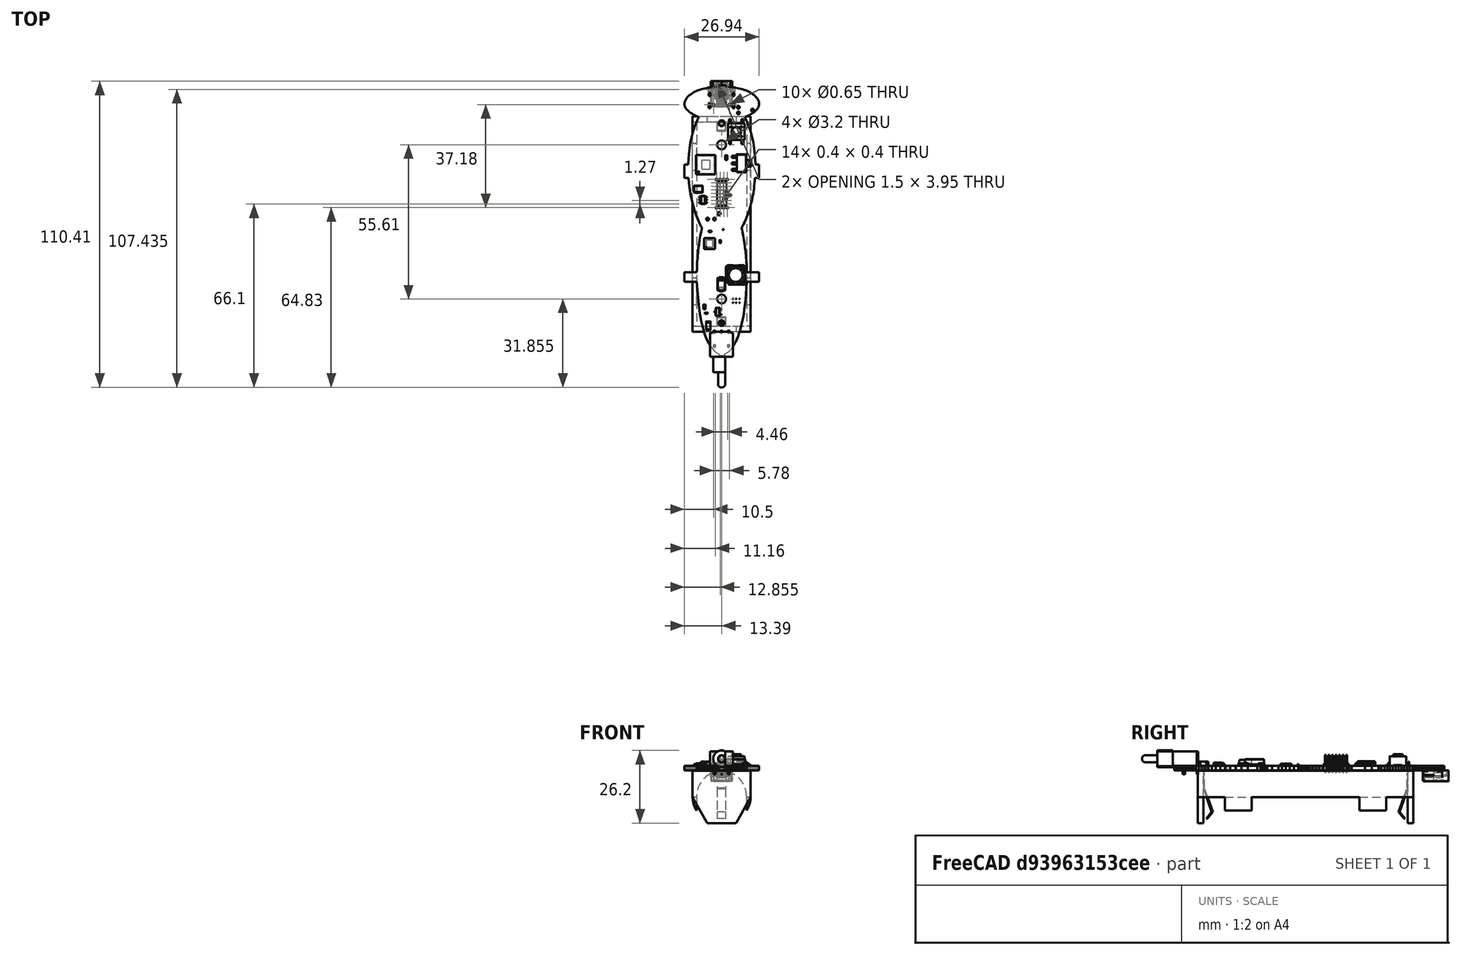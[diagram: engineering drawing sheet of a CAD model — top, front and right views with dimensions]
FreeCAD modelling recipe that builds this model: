
FCSTD DOCUMENT  (FreeCAD 0.21R30454 (Git))
Label: WholeBadge
License: All rights reserved
LicenseURL: http://en.wikipedia.org/wiki/All_rights_reserved
objects: App::Link×64, Part::Feature×20, App::Part×5, PartDesign::CoordinateSystem×1, Sketcher::SketchObject×1
note: 22 computed .brp shape members not serialized (recipe doc carries the construction recipe); baked Part::Feature solids carry a one-line shape summary decoded from their .brp

FEATURE [PartDesign::CoordinateSystem] Local_CS_931
  AttacherType = Attacher::AttachEngine3D
  MapMode = 2
  Support = -> [X_Axis001]
FEATURE [Part::Feature] Pcb_931
  shape: bbox 26.94 x 97.45 x 1.6 mm, 316 faces (baked)
FEATURE [Sketcher::SketchObject] PCB_Sketch_931
  FullyConstrained = false
  sketch-geometry (258):
    g0: LineSegment StartX=204.611 StartY=-59.7706 StartZ=0 EndX=204.161 EndY=-58.747 EndZ=0
    g1: LineSegment StartX=207.307 StartY=-79.6422 StartZ=0 EndX=208.849 EndY=-79.6422 EndZ=0
    g2: LineSegment StartX=203.133 StartY=-100.504 StartZ=0 EndX=202.842 EndY=-99.0355 EndZ=0
    g3: LineSegment StartX=198.204 StartY=-141.964 StartZ=0 EndX=198.335 EndY=-141.829 EndZ=0
    g4: LineSegment StartX=196.821 StartY=-46.2543 StartZ=0 EndX=195.381 EndY=-46.2543 EndZ=0
    g5: LineSegment StartX=186.994 StartY=-104.828 StartZ=0 EndX=186.849 EndY=-106.147 EndZ=0
    g6: LineSegment StartX=190.699 StartY=-139.374 StartZ=0 EndX=191.002 EndY=-139.905 EndZ=0
    g7: LineSegment StartX=194.282 StartY=-143.161 StartZ=0 EndX=194.282 EndY=-143.702 EndZ=0
    g8: LineSegment StartX=206.155 StartY=-49.1673 StartZ=0 EndX=205.642 EndY=-48.8567 EndZ=0
    g9: LineSegment StartX=207.546 StartY=-55.4632 StartZ=0 EndX=207.833 EndY=-55.1801 EndZ=0
    g10: LineSegment StartX=191.879 StartY=-141.193 StartZ=0 EndX=192.157 EndY=-141.532 EndZ=0
    g11: LineSegment StartX=186.361 StartY=-117.075 StartZ=0 EndX=186.651 EndY=-121.509 EndZ=0
    g12: LineSegment StartX=208.789 StartY=-53.5041 StartZ=0 EndX=208.834 EndY=-53.2317 EndZ=0
    g13: LineSegment StartX=206.019 StartY=-88.581 StartZ=0 EndX=206.204 EndY=-87.8001 EndZ=0
    g14: LineSegment StartX=203.931 StartY=-123.5 StartZ=0 EndX=204.11 EndY=-121.509 EndZ=0
    g15: LineSegment StartX=183.585 StartY=-81.6183 StartZ=0 EndX=183.791 EndY=-83.5056 EndZ=0
    g16: LineSegment StartX=201.902 StartY=-134.849 StartZ=0 EndX=202.197 EndY=-133.815 EndZ=0
    g17: LineSegment StartX=202.746 StartY=-97.2753 StartZ=0 EndX=202.978 EndY=-96.8717 EndZ=0
    g18: LineSegment StartX=202.76 StartY=-131.45 StartZ=0 EndX=203.025 EndY=-130.106 EndZ=0
    g19: LineSegment StartX=184.261 StartY=-65.7953 StartZ=0 EndX=184.058 EndY=-66.826 EndZ=0
    g20: LineSegment StartX=202.505 StartY=-97.6016 StartZ=0 EndX=202.585 EndY=-97.5204 EndZ=0
    g21: LineSegment StartX=196.48 StartY=-143.161 StartZ=0 EndX=196.623 EndY=-143.098 EndZ=0
    g22: LineSegment StartX=185.289 StartY=-56.8742 StartZ=0 EndX=185.841 EndY=-57.153 EndZ=0
    g23: LineSegment StartX=208.834 StartY=-53.2317 StartZ=0 EndX=208.851 EndY=-52.9624 EndZ=0
    g24: LineSegment StartX=204.4 StartY=-117.075 StartZ=0 EndX=208.849 EndY=-117.075 EndZ=0
    g25: LineSegment StartX=185.651 StartY=-48.576 StartZ=0 EndX=185.119 EndY=-48.8567 EndZ=0
    g26: LineSegment StartX=200.369 StartY=-138.788 StartZ=0 EndX=200.678 EndY=-138.143 EndZ=0
    g27: LineSegment StartX=185.964 StartY=-92.6642 StartZ=0 EndX=186.78 EndY=-94.7637 EndZ=0
    g28: LineSegment StartX=198.468 StartY=-141.686 StartZ=0 EndX=198.604 EndY=-141.532 EndZ=0
    g29: LineSegment StartX=200.262 StartY=-47.1518 StartZ=0 EndX=199.594 EndY=-47.0453 EndZ=0
    g30: LineSegment StartX=186.393 StartY=-112.527 StartZ=0 EndX=186.377 EndY=-113.724 EndZ=0
    g31: LineSegment StartX=182.209 StartY=-51.6716 StartZ=0 EndX=182.103 EndY=-51.9211 EndZ=0
    g32: LineSegment StartX=187.169 StartY=-103.429 StartZ=0 EndX=186.994 EndY=-104.828 EndZ=0
    g33: LineSegment StartX=197.156 StartY=-142.81 StartZ=0 EndX=197.366 EndY=-142.672 EndZ=0
    g34: LineSegment StartX=203.992 StartY=-48.0954 StartZ=0 EndX=203.408 EndY=-47.8915 EndZ=0
    g35: LineSegment StartX=200.678 StartY=-138.143 StartZ=0 EndX=200.987 EndY=-137.433 EndZ=0
    g36: LineSegment StartX=191.301 StartY=-140.383 StartZ=0 EndX=191.593 EndY=-140.811 EndZ=0
    g37: LineSegment StartX=186.503 StartY=-110.129 StartZ=0 EndX=186.46 EndY=-110.807 EndZ=0
    g38: LineSegment StartX=183.377 StartY=-72.3896 StartZ=0 EndX=183.215 EndY=-74.8986 EndZ=0
    g39: LineSegment StartX=206.647 StartY=-49.5098 StartZ=0 EndX=206.155 EndY=-49.1673 EndZ=0
    g40: LineSegment StartX=201.601 StartY=-135.792 StartZ=0 EndX=201.902 EndY=-134.849 EndZ=0
    g41: LineSegment StartX=203.408 StartY=-47.8915 StartZ=0 EndX=202.807 EndY=-47.709 EndZ=0
    g42: LineSegment StartX=208.428 StartY=-51.4271 StartZ=0 EndX=208.284 EndY=-51.188 EndZ=0
    g43: LineSegment StartX=182.294 StartY=-54.3351 StartZ=0 EndX=182.469 EndY=-54.6157 EndZ=0
    g44: LineSegment StartX=185.119 StartY=-48.8567 StartZ=0 EndX=184.607 EndY=-49.1673 EndZ=0
    g45: LineSegment StartX=204.382 StartY=-93.7798 StartZ=0 EndX=204.798 EndY=-92.6642 EndZ=0
    g46: LineSegment StartX=183.215 StartY=-74.8986 StartZ=0 EndX=181.912 EndY=-74.8986 EndZ=0
    g47: LineSegment StartX=205.216 StartY=-91.4223 StartZ=0 EndX=205.627 EndY=-90.0595 EndZ=0
    g48: LineSegment StartX=208.849 StartY=-74.8986 StartZ=0 EndX=207.546 EndY=-74.8986 EndZ=0
    g49: LineSegment StartX=186.651 StartY=-121.509 StartZ=0 EndX=187.031 EndY=-125.349 EndZ=0
    g50: LineSegment StartX=204.125 StartY=-108.431 StartZ=0 EndX=203.913 EndY=-106.147 EndZ=0
    g51: LineSegment StartX=187.38 StartY=-101.978 StartZ=0 EndX=187.169 EndY=-103.429 EndZ=0
    g52: LineSegment StartX=183.913 StartY=-56.0295 StartZ=0 EndX=184.326 EndY=-56.3121 EndZ=0
    g53: LineSegment StartX=205.11 StartY=-48.576 StartZ=0 EndX=204.56 EndY=-48.3229 EndZ=0
    g54: LineSegment StartX=201.561 StartY=-47.4 StartZ=0 EndX=200.918 EndY=-47.2693 EndZ=0
    g55: LineSegment StartX=204.258 StartY=-110.129 StartZ=0 EndX=204.2 EndY=-109.347 EndZ=0
    g56: LineSegment StartX=193.978 StartY=-143.02 StartZ=0 EndX=194.282 EndY=-143.161 EndZ=0
    g57: LineSegment StartX=181.958 StartY=-52.4338 StartZ=0 EndX=181.922 EndY=-52.6963 EndZ=0
    g58: LineSegment StartX=204.798 StartY=-92.6642 StartZ=0 EndX=205.216 EndY=-91.4223 EndZ=0
    g59: LineSegment StartX=204.302 StartY=-110.807 StartZ=0 EndX=204.258 EndY=-110.129 EndZ=0
    g60: LineSegment StartX=196.623 StartY=-143.098 StartZ=0 EndX=196.784 EndY=-143.02 EndZ=0
    g61: LineSegment StartX=198.227 StartY=-46.857 StartZ=0 EndX=196.821 EndY=-46.6878 EndZ=0
    g62: LineSegment StartX=204.56 StartY=-48.3229 StartZ=0 EndX=203.992 EndY=-48.0954 EndZ=0
    g63: LineSegment StartX=183.726 StartY=-68.9546 StartZ=0 EndX=183.593 EndY=-70.0623 EndZ=0
    g64: LineSegment StartX=200.215 StartY=-139.088 StartZ=0 EndX=200.369 EndY=-138.788 EndZ=0
    g65: LineSegment StartX=207.117 StartY=-49.8853 StartZ=0 EndX=206.647 EndY=-49.5098 EndZ=0
    g66: LineSegment StartX=181.972 StartY=-53.5041 StartZ=0 EndX=182.047 EndY=-53.779 EndZ=0
    g67: LineSegment StartX=184.607 StartY=-49.1673 StartZ=0 EndX=184.114 EndY=-49.5098 EndZ=0
    g68: LineSegment StartX=199.61 StartY=-140.15 StartZ=0 EndX=199.759 EndY=-139.905 EndZ=0
    g69: LineSegment StartX=205.627 StartY=-90.0595 StartZ=0 EndX=206.019 EndY=-88.581 EndZ=0
    g70: LineSegment StartX=202.679 StartY=-98.3125 StartZ=0 EndX=202.505 EndY=-97.6016 EndZ=0
    g71: LineSegment StartX=196.962 StartY=-142.925 StartZ=0 EndX=197.156 EndY=-142.81 EndZ=0
    g72: LineSegment StartX=206.204 StartY=-87.8001 StartZ=0 EndX=206.381 EndY=-86.9923 EndZ=0
    g73: LineSegment StartX=198.604 StartY=-141.532 StartZ=0 EndX=198.742 EndY=-141.368 EndZ=0
    g74: LineSegment StartX=189.774 StartY=-137.433 StartZ=0 EndX=190.393 EndY=-138.788 EndZ=0
    g75: LineSegment StartX=184.058 StartY=-66.826 StartZ=0 EndX=183.88 EndY=-67.8774 EndZ=0
    g76: LineSegment StartX=189.16 StartY=-135.792 StartZ=0 EndX=189.774 EndY=-137.433 EndZ=0
    g77: LineSegment StartX=186.151 StartY=-59.7706 StartZ=0 EndX=185.743 EndY=-60.7805 EndZ=0
    g78: LineSegment StartX=206.381 StartY=-86.9923 StartZ=0 EndX=206.547 EndY=-86.1583 EndZ=0
    g79: LineSegment StartX=208.84 StartY=-52.6963 StartZ=0 EndX=208.803 EndY=-52.4338 EndZ=0
    g80: LineSegment StartX=204.318 StartY=-57.4299 StartZ=0 EndX=204.92 EndY=-57.153 EndZ=0
    g81: LineSegment StartX=188.015 StartY=-97.2753 StartZ=0 EndX=188.257 EndY=-97.6016 EndZ=0
    g82: LineSegment StartX=205.472 StartY=-56.8742 StartZ=0 EndX=205.977 EndY=-56.5938 EndZ=0
    g83: LineSegment StartX=185.134 StartY=-90.0595 StartZ=0 EndX=185.545 EndY=-91.4223 EndZ=0
    g84: LineSegment StartX=203.512 StartY=-127.062 StartZ=0 EndX=203.731 EndY=-125.349 EndZ=0
    g85: LineSegment StartX=202.807 StartY=-47.709 StartZ=0 EndX=202.191 EndY=-47.5458 EndZ=0
    g86: LineSegment StartX=189.843 StartY=-47.2693 StartZ=0 EndX=189.2 EndY=-47.4 EndZ=0
    g87: LineSegment StartX=203.025 StartY=-130.106 StartZ=0 EndX=203.276 EndY=-128.645 EndZ=0
    g88: LineSegment StartX=199.314 StartY=-140.603 StartZ=0 EndX=199.461 EndY=-140.383 EndZ=0
    g89: LineSegment StartX=207.169 StartY=-70.0623 StartZ=0 EndX=207.035 EndY=-68.9546 EndZ=0
    g90: LineSegment StartX=199.461 StartY=-140.383 StartZ=0 EndX=199.61 EndY=-140.15 EndZ=0
    g91: LineSegment StartX=191.002 StartY=-139.905 StartZ=0 EndX=191.301 EndY=-140.383 EndZ=0
    g92: LineSegment StartX=186.46 StartY=-110.807 StartZ=0 EndX=186.429 EndY=-111.412 EndZ=0
    g93: LineSegment StartX=182.638 StartY=-50.9546 StartZ=0 EndX=182.477 EndY=-51.188 EndZ=0
    g94: LineSegment StartX=196.821 StartY=-46.6878 StartZ=0 EndX=196.821 EndY=-46.2543 EndZ=0
    g95: LineSegment StartX=183.543 StartY=-55.7465 StartZ=0 EndX=183.913 EndY=-56.0295 EndZ=0
    g96: LineSegment StartX=181.912 StartY=-117.075 StartZ=0 EndX=186.361 EndY=-117.075 EndZ=0
    g97: LineSegment StartX=204.2 StartY=-109.347 StartZ=0 EndX=204.125 EndY=-108.431 EndZ=0
    g98: LineSegment StartX=181.911 StartY=-52.9624 StartZ=0 EndX=181.927 EndY=-53.2317 EndZ=0
    g99: LineSegment StartX=206.702 StartY=-85.2987 StartZ=0 EndX=206.844 EndY=-84.4142 EndZ=0
    g100: LineSegment StartX=208.742 StartY=-52.1753 StartZ=0 EndX=208.658 EndY=-51.9211 EndZ=0
    g101: LineSegment StartX=192.686 StartY=-142.089 StartZ=0 EndX=192.935 EndY=-142.314 EndZ=0
    g102: LineSegment StartX=187.095 StartY=-57.7046 StartZ=0 EndX=186.6 EndY=-58.747 EndZ=0
    g103: LineSegment StartX=208.849 StartY=-117.075 StartZ=0 EndX=208.849 EndY=-113.724 EndZ=0
    g104: LineSegment StartX=196.784 StartY=-143.02 StartZ=0 EndX=196.962 EndY=-142.925 EndZ=0
    g105: LineSegment StartX=186.6 StartY=-58.747 StartZ=0 EndX=186.151 EndY=-59.7706 EndZ=0
    g106: LineSegment StartX=184.785 StartY=-56.5938 StartZ=0 EndX=185.289 EndY=-56.8742 EndZ=0
    g107: LineSegment StartX=198.882 StartY=-141.193 StartZ=0 EndX=199.024 EndY=-141.008 EndZ=0
    g108: LineSegment StartX=191.167 StartY=-47.0453 StartZ=0 EndX=189.843 EndY=-47.2693 EndZ=0
    g109: LineSegment StartX=182.103 StartY=-51.9211 StartZ=0 EndX=182.019 EndY=-52.1753 EndZ=0
    g110: LineSegment StartX=200.918 StartY=-47.2693 StartZ=0 EndX=200.262 EndY=-47.1518 EndZ=0
    g111: LineSegment StartX=203.268 StartY=-96.315 StartZ=0 EndX=203.607 EndY=-95.6105 EndZ=0
    g112: LineSegment StartX=188.565 StartY=-133.815 StartZ=0 EndX=189.16 EndY=-135.792 EndZ=0
    g113: LineSegment StartX=207.218 StartY=-55.7465 StartZ=0 EndX=207.546 EndY=-55.4632 EndZ=0
    g114: LineSegment StartX=207.252 StartY=-80.641 StartZ=0 EndX=207.307 EndY=-79.6422 EndZ=0
    g115: LineSegment StartX=188.257 StartY=-97.6016 StartZ=0 EndX=187.92 EndY=-99.0355 EndZ=0
    g116: LineSegment StartX=186.443 StartY=-57.4299 StartZ=0 EndX=187.095 EndY=-57.7046 EndZ=0
    g117: LineSegment StartX=203.607 StartY=-95.6105 StartZ=0 EndX=203.982 EndY=-94.7637 EndZ=0
    g118: LineSegment StartX=207.554 StartY=-50.2921 StartZ=0 EndX=207.117 EndY=-49.8853 EndZ=0
    g119: LineSegment StartX=185.841 StartY=-57.153 StartZ=0 EndX=186.443 EndY=-57.4299 EndZ=0
    g120: LineSegment StartX=204.267 StartY=-119.37 StartZ=0 EndX=204.4 EndY=-117.075 EndZ=0
    g121: LineSegment StartX=199.168 StartY=-140.811 StartZ=0 EndX=199.314 EndY=-140.603 EndZ=0
    g122: LineSegment StartX=199.91 StartY=-139.646 StartZ=0 EndX=200.062 EndY=-139.374 EndZ=0
    g123: LineSegment StartX=203.731 StartY=-125.349 StartZ=0 EndX=203.931 EndY=-123.5 EndZ=0
    g124: LineSegment StartX=206.844 StartY=-84.4142 StartZ=0 EndX=206.971 EndY=-83.5056 EndZ=0
    g125: LineSegment StartX=203.913 StartY=-106.147 StartZ=0 EndX=203.768 EndY=-104.828 EndZ=0
    g126: LineSegment StartX=206.848 StartY=-56.0295 StartZ=0 EndX=207.218 EndY=-55.7465 EndZ=0
    g127: LineSegment StartX=198.335 StartY=-141.829 StartZ=0 EndX=198.468 EndY=-141.686 EndZ=0
    g128: LineSegment StartX=204.333 StartY=-111.412 StartZ=0 EndX=204.302 EndY=-110.807 EndZ=0
    g129: LineSegment StartX=183.004 StartY=-50.5063 StartZ=0 EndX=182.814 EndY=-50.7272 EndZ=0
    g130: LineSegment StartX=183.88 StartY=-67.8774 StartZ=0 EndX=183.726 EndY=-68.9546 EndZ=0
    g131: LineSegment StartX=181.912 StartY=-79.6422 StartZ=0 EndX=183.454 EndY=-79.6422 EndZ=0
    g132: LineSegment StartX=198.075 StartY=-142.089 StartZ=0 EndX=198.204 EndY=-141.964 EndZ=0
    g133: LineSegment StartX=200.062 StartY=-139.374 StartZ=0 EndX=200.215 EndY=-139.088 EndZ=0
    g134: LineSegment StartX=185.545 StartY=-91.4223 StartZ=0 EndX=185.964 EndY=-92.6642 EndZ=0
    g135: LineSegment StartX=202.978 StartY=-96.8717 StartZ=0 EndX=203.268 EndY=-96.315 EndZ=0
    g136: LineSegment StartX=205.018 StartY=-60.7805 StartZ=0 EndX=204.611 EndY=-59.7706 EndZ=0
    g137: LineSegment StartX=187.954 StartY=-47.709 StartZ=0 EndX=187.354 EndY=-47.8915 EndZ=0
    g138: LineSegment StartX=208.292 StartY=-54.6157 StartZ=0 EndX=208.467 EndY=-54.3351 EndZ=0
    g139: LineSegment StartX=187.92 StartY=-99.0355 StartZ=0 EndX=187.629 EndY=-100.504 EndZ=0
    g140: LineSegment StartX=208.658 StartY=-51.9211 StartZ=0 EndX=208.553 EndY=-51.6716 EndZ=0
    g141: LineSegment StartX=188.002 StartY=-131.45 StartZ=0 EndX=188.565 EndY=-133.815 EndZ=0
    g142: LineSegment StartX=204.11 StartY=-121.509 StartZ=0 EndX=204.267 EndY=-119.37 EndZ=0
    g143: LineSegment StartX=196.48 StartY=-143.702 StartZ=0 EndX=196.48 EndY=-143.161 EndZ=0
    g144: LineSegment StartX=183.791 StartY=-83.5056 StartZ=0 EndX=184.059 EndY=-85.2987 EndZ=0
    g145: LineSegment StartX=193.605 StartY=-142.81 StartZ=0 EndX=193.8 EndY=-142.925 EndZ=0
    g146: LineSegment StartX=186.636 StartY=-108.431 StartZ=0 EndX=186.503 EndY=-110.129 EndZ=0
    g147: LineSegment StartX=192.535 StartY=-46.857 StartZ=0 EndX=191.167 EndY=-47.0453 EndZ=0
    g148: LineSegment StartX=198.742 StartY=-141.368 StartZ=0 EndX=198.882 EndY=-141.193 EndZ=0
    g149: LineSegment StartX=182.814 StartY=-50.7272 StartZ=0 EndX=182.638 EndY=-50.9546 EndZ=0
    g150: LineSegment StartX=187.031 StartY=-125.349 StartZ=0 EndX=187.486 EndY=-128.645 EndZ=0
    g151: LineSegment StartX=183.421 StartY=-50.085 StartZ=0 EndX=183.207 EndY=-50.2921 EndZ=0
    g152: LineSegment StartX=204.368 StartY=-112.527 StartZ=0 EndX=204.354 EndY=-111.975 EndZ=0
    g153: LineSegment StartX=202.585 StartY=-97.5204 StartZ=0 EndX=202.746 EndY=-97.2753 EndZ=0
    g154: LineSegment StartX=184.742 StartY=-88.581 StartZ=0 EndX=185.134 EndY=-90.0595 EndZ=0
    g155: LineSegment StartX=183.454 StartY=-79.6422 StartZ=0 EndX=183.585 EndY=-81.6183 EndZ=0
    g156: LineSegment StartX=206.971 StartY=-83.5056 StartZ=0 EndX=207.082 EndY=-82.5734 EndZ=0
    g157: LineSegment StartX=206.704 StartY=-66.826 StartZ=0 EndX=206.501 EndY=-65.7953 EndZ=0
    g158: LineSegment StartX=203.592 StartY=-103.429 StartZ=0 EndX=203.382 EndY=-101.978 EndZ=0
    g159: LineSegment StartX=208.714 StartY=-53.779 StartZ=0 EndX=208.789 EndY=-53.5041 EndZ=0
    g160: LineSegment StartX=203.276 StartY=-128.645 StartZ=0 EndX=203.512 EndY=-127.062 EndZ=0
    g161: LineSegment StartX=186.429 StartY=-111.412 StartZ=0 EndX=186.393 EndY=-112.527 EndZ=0
    g162: LineSegment StartX=197.826 StartY=-142.314 StartZ=0 EndX=198.075 EndY=-142.089 EndZ=0
    g163: LineSegment StartX=193.396 StartY=-142.672 StartZ=0 EndX=193.605 EndY=-142.81 EndZ=0
    g164: LineSegment StartX=208.851 StartY=-52.9624 StartZ=0 EndX=208.84 EndY=-52.6963 EndZ=0
    g165: LineSegment StartX=197.59 StartY=-142.507 StartZ=0 EndX=197.826 EndY=-142.314 EndZ=0
    g166: LineSegment StartX=206.009 StartY=-63.7765 StartZ=0 EndX=205.715 EndY=-62.7784 EndZ=0
    g167: LineSegment StartX=185.743 StartY=-60.7805 StartZ=0 EndX=185.376 EndY=-61.7814 EndZ=0
    g168: LineSegment StartX=195.381 StartY=-143.702 StartZ=0 EndX=196.48 EndY=-143.702 EndZ=0
    g169: LineSegment StartX=183.593 StartY=-70.0623 StartZ=0 EndX=183.377 EndY=-72.3896 EndZ=0
    g170: LineSegment StartX=206.501 StartY=-65.7953 StartZ=0 EndX=206.27 EndY=-64.7804 EndZ=0
    g171: LineSegment StartX=200.987 StartY=-137.433 StartZ=0 EndX=201.296 EndY=-136.651 EndZ=0
    g172: LineSegment StartX=191.593 StartY=-140.811 StartZ=0 EndX=191.879 EndY=-141.193 EndZ=0
    g173: LineSegment StartX=182.154 StartY=-54.0561 StartZ=0 EndX=182.294 EndY=-54.3351 EndZ=0
    g174: LineSegment StartX=208.607 StartY=-54.0561 StartZ=0 EndX=208.714 EndY=-53.779 EndZ=0
    g175: LineSegment StartX=182.047 StartY=-53.779 StartZ=0 EndX=182.154 EndY=-54.0561 EndZ=0
    g176: LineSegment StartX=199.024 StartY=-141.008 StartZ=0 EndX=199.168 EndY=-140.811 EndZ=0
    g177: LineSegment StartX=192.935 StartY=-142.314 StartZ=0 EndX=193.172 EndY=-142.507 EndZ=0
    g178: LineSegment StartX=189.2 StartY=-47.4 StartZ=0 EndX=188.57 EndY=-47.5458 EndZ=0
    g179: LineSegment StartX=182.68 StartY=-54.8975 StartZ=0 EndX=182.928 EndY=-55.1801 EndZ=0
    g180: LineSegment StartX=186.377 StartY=-113.724 StartZ=0 EndX=181.912 EndY=-113.724 EndZ=0
    g181: LineSegment StartX=202.483 StartY=-132.685 StartZ=0 EndX=202.76 EndY=-131.45 EndZ=0
    g182: LineSegment StartX=183.216 StartY=-55.4632 StartZ=0 EndX=183.543 EndY=-55.7465 EndZ=0
    g183: LineSegment StartX=206.435 StartY=-56.3121 StartZ=0 EndX=206.848 EndY=-56.0295 EndZ=0
    g184: LineSegment StartX=184.326 StartY=-56.3121 StartZ=0 EndX=184.785 EndY=-56.5938 EndZ=0
    g185: LineSegment StartX=184.753 StartY=-63.7765 StartZ=0 EndX=184.492 EndY=-64.7804 EndZ=0
    g186: LineSegment StartX=206.27 StartY=-64.7804 StartZ=0 EndX=206.009 EndY=-63.7765 EndZ=0
    g187: LineSegment StartX=186.202 StartY=-48.3229 StartZ=0 EndX=185.651 EndY=-48.576 EndZ=0
    g188: LineSegment StartX=205.385 StartY=-61.7814 StartZ=0 EndX=205.018 EndY=-60.7805 EndZ=0
    g189: LineSegment StartX=208.467 StartY=-54.3351 StartZ=0 EndX=208.607 EndY=-54.0561 EndZ=0
    g190: LineSegment StartX=187.629 StartY=-100.504 StartZ=0 EndX=187.38 EndY=-101.978 EndZ=0
    g191: LineSegment StartX=207.176 StartY=-81.6183 StartZ=0 EndX=207.252 EndY=-80.641 EndZ=0
    g192: LineSegment StartX=208.082 StartY=-54.8975 StartZ=0 EndX=208.292 EndY=-54.6157 EndZ=0
    g193: LineSegment StartX=204.385 StartY=-113.724 StartZ=0 EndX=204.368 EndY=-112.527 EndZ=0
    g194: LineSegment StartX=208.849 StartY=-113.724 StartZ=0 EndX=204.385 EndY=-113.724 EndZ=0
    g195: LineSegment StartX=201.296 StartY=-136.651 StartZ=0 EndX=201.601 EndY=-135.792 EndZ=0
    g196: LineSegment StartX=183.207 StartY=-50.2921 StartZ=0 EndX=183.004 EndY=-50.5063 EndZ=0
    g197: LineSegment StartX=188.57 StartY=-47.5458 StartZ=0 EndX=187.954 EndY=-47.709 EndZ=0
    g198: LineSegment StartX=190.393 StartY=-138.788 StartZ=0 EndX=190.699 EndY=-139.374 EndZ=0
    g199: LineSegment StartX=185.047 StartY=-62.7784 StartZ=0 EndX=184.753 EndY=-63.7765 EndZ=0
    g200: LineSegment StartX=199.594 StartY=-47.0453 StartZ=0 EndX=198.227 EndY=-46.857 EndZ=0
    g201: LineSegment StartX=204.92 StartY=-57.153 StartZ=0 EndX=205.472 EndY=-56.8742 EndZ=0
    g202: LineSegment StartX=207.546 StartY=-74.8986 StartZ=0 EndX=207.384 EndY=-72.3896 EndZ=0
    g203: LineSegment StartX=208.849 StartY=-79.6422 StartZ=0 EndX=208.849 EndY=-74.8986 EndZ=0
    g204: LineSegment StartX=203.382 StartY=-101.978 StartZ=0 EndX=203.133 EndY=-100.504 EndZ=0
    g205: LineSegment StartX=205.977 StartY=-56.5938 StartZ=0 EndX=206.435 EndY=-56.3121 EndZ=0
    g206: LineSegment StartX=185.376 StartY=-61.7814 StartZ=0 EndX=185.047 EndY=-62.7784 EndZ=0
    g207: LineSegment StartX=184.38 StartY=-86.9923 StartZ=0 EndX=184.742 EndY=-88.581 EndZ=0
    g208: LineSegment StartX=193.8 StartY=-142.925 StartZ=0 EndX=193.978 EndY=-143.02 EndZ=0
    g209: LineSegment StartX=181.912 StartY=-74.8986 StartZ=0 EndX=181.912 EndY=-79.6422 EndZ=0
    g210: LineSegment StartX=182.334 StartY=-51.4271 StartZ=0 EndX=182.209 EndY=-51.6716 EndZ=0
    g211: LineSegment StartX=195.381 StartY=-46.2543 StartZ=0 EndX=193.94 EndY=-46.2543 EndZ=0
    g212: LineSegment StartX=181.922 StartY=-52.6963 StartZ=0 EndX=181.911 EndY=-52.9624 EndZ=0
    g213: LineSegment StartX=192.427 StartY=-141.829 StartZ=0 EndX=192.686 EndY=-142.089 EndZ=0
    g214: LineSegment StartX=208.284 StartY=-51.188 StartZ=0 EndX=208.123 EndY=-50.9546 EndZ=0
    g215: LineSegment StartX=186.769 StartY=-48.0954 StartZ=0 EndX=186.202 EndY=-48.3229 EndZ=0
    g216: LineSegment StartX=202.191 StartY=-47.5458 StartZ=0 EndX=201.561 EndY=-47.4 EndZ=0
    g217: LineSegment StartX=183.644 StartY=-49.8853 StartZ=0 EndX=183.421 EndY=-50.085 EndZ=0
    g218: LineSegment StartX=187.354 StartY=-47.8915 StartZ=0 EndX=186.769 EndY=-48.0954 EndZ=0
    g219: LineSegment StartX=197.366 StartY=-142.672 StartZ=0 EndX=197.59 EndY=-142.507 EndZ=0
    g220: LineSegment StartX=207.947 StartY=-50.7272 StartZ=0 EndX=207.554 EndY=-50.2921 EndZ=0
    g221: LineSegment StartX=187.493 StartY=-96.315 StartZ=0 EndX=188.015 EndY=-97.2753 EndZ=0
    g222: LineSegment StartX=192.157 StartY=-141.532 StartZ=0 EndX=192.427 EndY=-141.829 EndZ=0
    g223: LineSegment StartX=184.059 StartY=-85.2987 StartZ=0 EndX=184.38 EndY=-86.9923 EndZ=0
    g224: LineSegment StartX=181.927 StartY=-53.2317 StartZ=0 EndX=181.972 EndY=-53.5041 EndZ=0
    g225: LineSegment StartX=202.197 StartY=-133.815 StartZ=0 EndX=202.483 EndY=-132.685 EndZ=0
    g226: LineSegment StartX=194.282 StartY=-143.702 StartZ=0 EndX=195.381 EndY=-143.702 EndZ=0
    g227: LineSegment StartX=203.982 StartY=-94.7637 StartZ=0 EndX=204.382 EndY=-93.7798 EndZ=0
    g228: LineSegment StartX=184.492 StartY=-64.7804 StartZ=0 EndX=184.261 EndY=-65.7953 EndZ=0
    g229: LineSegment StartX=193.172 StartY=-142.507 StartZ=0 EndX=193.396 EndY=-142.672 EndZ=0
    g230: LineSegment StartX=182.928 StartY=-55.1801 StartZ=0 EndX=183.216 EndY=-55.4632 EndZ=0
    g231: LineSegment StartX=204.161 StartY=-58.747 StartZ=0 EndX=203.666 EndY=-57.7046 EndZ=0
    g232: LineSegment StartX=182.477 StartY=-51.188 StartZ=0 EndX=182.334 EndY=-51.4271 EndZ=0
    g233: LineSegment StartX=199.759 StartY=-139.905 StartZ=0 EndX=199.91 EndY=-139.646 EndZ=0
    g234: LineSegment StartX=187.486 StartY=-128.645 StartZ=0 EndX=188.002 EndY=-131.45 EndZ=0
    g235: LineSegment StartX=205.642 StartY=-48.8567 StartZ=0 EndX=205.11 EndY=-48.576 EndZ=0
    g236: LineSegment StartX=207.035 StartY=-68.9546 StartZ=0 EndX=206.881 EndY=-67.8774 EndZ=0
    g237: LineSegment StartX=181.912 StartY=-113.724 StartZ=0 EndX=181.912 EndY=-117.075 EndZ=0
    g238: LineSegment StartX=208.553 StartY=-51.6716 StartZ=0 EndX=208.428 EndY=-51.4271 EndZ=0
    g239: LineSegment StartX=202.842 StartY=-99.0355 StartZ=0 EndX=202.679 EndY=-98.3125 EndZ=0
    g240: LineSegment StartX=207.384 StartY=-72.3896 StartZ=0 EndX=207.169 EndY=-70.0623 EndZ=0
    g241: LineSegment StartX=186.849 StartY=-106.147 StartZ=0 EndX=186.636 EndY=-108.431 EndZ=0
    g242: LineSegment StartX=208.803 StartY=-52.4338 StartZ=0 EndX=208.742 EndY=-52.1753 EndZ=0
    g243: LineSegment StartX=182.469 StartY=-54.6157 StartZ=0 EndX=182.68 EndY=-54.8975 EndZ=0
    g244: LineSegment StartX=182.019 StartY=-52.1753 StartZ=0 EndX=181.958 EndY=-52.4338 EndZ=0
    g245: LineSegment StartX=203.768 StartY=-104.828 StartZ=0 EndX=203.592 EndY=-103.429 EndZ=0
    g246: LineSegment StartX=206.547 StartY=-86.1583 StartZ=0 EndX=206.702 EndY=-85.2987 EndZ=0
    g247: LineSegment StartX=207.082 StartY=-82.5734 StartZ=0 EndX=207.176 EndY=-81.6183 EndZ=0
    g248: LineSegment StartX=184.114 StartY=-49.5098 StartZ=0 EndX=183.644 EndY=-49.8853 EndZ=0
    g249: LineSegment StartX=207.833 StartY=-55.1801 StartZ=0 EndX=208.082 EndY=-54.8975 EndZ=0
    g250: LineSegment StartX=193.94 StartY=-46.2543 StartZ=0 EndX=193.94 EndY=-46.6878 EndZ=0
    g251: LineSegment StartX=206.881 StartY=-67.8774 StartZ=0 EndX=206.704 EndY=-66.826 EndZ=0
    g252: LineSegment StartX=186.78 StartY=-94.7637 StartZ=0 EndX=187.493 EndY=-96.315 EndZ=0
    g253: LineSegment StartX=204.354 StartY=-111.975 StartZ=0 EndX=204.333 EndY=-111.412 EndZ=0
    g254: LineSegment StartX=203.666 StartY=-57.7046 StartZ=0 EndX=204.318 EndY=-57.4299 EndZ=0
    g255: LineSegment StartX=208.123 StartY=-50.9546 StartZ=0 EndX=207.947 EndY=-50.7272 EndZ=0
    g256: LineSegment StartX=205.715 StartY=-62.7784 StartZ=0 EndX=205.385 EndY=-61.7814 EndZ=0
    g257: LineSegment StartX=193.94 StartY=-46.6878 StartZ=0 EndX=192.535 EndY=-46.857 EndZ=0
  constraints (258):
    c: Coincident(g96,g237)
    c: Coincident(g180,g237)
    c: Coincident(g131,g209)
    c: Coincident(g46,g209)
    c: Coincident(g98,g212)
    c: Coincident(g98,g224)
    c: Coincident(g57,g212)
    c: Coincident(g57,g244)
    c: Coincident(g66,g224)
    c: Coincident(g109,g244)
    c: Coincident(g66,g175)
    c: Coincident(g31,g109)
    c: Coincident(g173,g175)
    c: Coincident(g31,g210)
    c: Coincident(g43,g173)
    c: Coincident(g210,g232)
    c: Coincident(g43,g243)
    c: Coincident(g93,g232)
    c: Coincident(g93,g149)
    c: Coincident(g179,g243)
    c: Coincident(g129,g149)
    c: Coincident(g179,g230)
    c: Coincident(g129,g196)
    c: Coincident(g38,g46)
    c: Coincident(g182,g230)
    c: Coincident(g151,g196)
    c: Coincident(g38,g169)
    c: Coincident(g151,g217)
    c: Coincident(g131,g155)
    c: Coincident(g95,g182)
    c: Coincident(g15,g155)
    c: Coincident(g63,g169)
    c: Coincident(g217,g248)
    c: Coincident(g63,g130)
    c: Coincident(g15,g144)
    c: Coincident(g75,g130)
    c: Coincident(g52,g95)
    c: Coincident(g144,g223)
    c: Coincident(g19,g75)
    c: Coincident(g67,g248)
    c: Coincident(g19,g228)
    c: Coincident(g52,g184)
    c: Coincident(g207,g223)
    c: Coincident(g185,g228)
    c: Coincident(g44,g67)
    c: Coincident(g154,g207)
    c: Coincident(g185,g199)
    c: Coincident(g106,g184)
    c: Coincident(g199,g206)
    c: Coincident(g25,g44)
    c: Coincident(g83,g154)
    c: Coincident(g22,g106)
    c: Coincident(g167,g206)
    c: Coincident(g83,g134)
    c: Coincident(g25,g187)
    c: Coincident(g77,g167)
    c: Coincident(g22,g119)
    c: Coincident(g27,g134)
    c: Coincident(g77,g105)
    c: Coincident(g187,g215)
    c: Coincident(g11,g96)
    c: Coincident(g30,g180)
    c: Coincident(g30,g161)
    c: Coincident(g92,g161)
    c: Coincident(g116,g119)
    c: Coincident(g37,g92)
    c: Coincident(g37,g146)
    c: Coincident(g102,g105)
    c: Coincident(g146,g241)
    c: Coincident(g11,g49)
    c: Coincident(g215,g218)
    c: Coincident(g27,g252)
    c: Coincident(g5,g241)
    c: Coincident(g5,g32)
    c: Coincident(g49,g150)
    c: Coincident(g102,g116)
    c: Coincident(g32,g51)
    c: Coincident(g137,g218)
    c: Coincident(g51,g190)
    c: Coincident(g150,g234)
    c: Coincident(g221,g252)
    c: Coincident(g139,g190)
    c: Coincident(g115,g139)
    c: Coincident(g137,g197)
    c: Coincident(g141,g234)
    c: Coincident(g81,g221)
    c: Coincident(g81,g115)
    c: Coincident(g112,g141)
    c: Coincident(g178,g197)
    c: Coincident(g76,g112)
    c: Coincident(g86,g178)
    c: Coincident(g74,g76)
    c: Coincident(g86,g108)
    c: Coincident(g74,g198)
    c: Coincident(g6,g198)
    c: Coincident(g6,g91)
    c: Coincident(g108,g147)
    c: Coincident(g36,g91)
    c: Coincident(g36,g172)
    c: Coincident(g10,g172)
    c: Coincident(g10,g222)
    c: Coincident(g213,g222)
    c: Coincident(g147,g257)
    c: Coincident(g101,g213)
    c: Coincident(g101,g177)
    c: Coincident(g177,g229)
    c: Coincident(g163,g229)
    c: Coincident(g145,g163)
    c: Coincident(g145,g208)
    c: Coincident(g250,g257)
    c: Coincident(g211,g250)
    c: Coincident(g56,g208)
    c: Coincident(g7,g226)
    c: Coincident(g7,g56)
    c: Coincident(g168,g226)
    c: Coincident(g4,g211)
    c: Coincident(g143,g168)
    c: Coincident(g21,g143)
    c: Coincident(g21,g60)
    c: Coincident(g60,g104)
    c: Coincident(g61,g94)
    c: Coincident(g4,g94)
    c: Coincident(g71,g104)
    c: Coincident(g33,g71)
    c: Coincident(g33,g219)
    c: Coincident(g165,g219)
    c: Coincident(g162,g165)
    c: Coincident(g132,g162)
    c: Coincident(g3,g132)
    c: Coincident(g61,g200)
    c: Coincident(g3,g127)
    c: Coincident(g28,g127)
    c: Coincident(g28,g73)
    c: Coincident(g73,g148)
    c: Coincident(g107,g148)
    c: Coincident(g107,g176)
    c: Coincident(g121,g176)
    c: Coincident(g88,g121)
    c: Coincident(g88,g90)
    c: Coincident(g29,g200)
    c: Coincident(g68,g90)
    c: Coincident(g68,g233)
    c: Coincident(g122,g233)
    c: Coincident(g122,g133)
    c: Coincident(g64,g133)
    c: Coincident(g29,g110)
    c: Coincident(g26,g64)
    c: Coincident(g26,g35)
    c: Coincident(g54,g110)
    c: Coincident(g35,g171)
    c: Coincident(g171,g195)
    c: Coincident(g54,g216)
    c: Coincident(g40,g195)
    c: Coincident(g16,g40)
    c: Coincident(g16,g225)
    c: Coincident(g85,g216)
    c: Coincident(g181,g225)
    c: Coincident(g20,g70)
    c: Coincident(g20,g153)
    c: Coincident(g70,g239)
    c: Coincident(g17,g153)
    c: Coincident(g18,g181)
    c: Coincident(g41,g85)
    c: Coincident(g2,g239)
    c: Coincident(g17,g135)
    c: Coincident(g18,g87)
    c: Coincident(g2,g204)
    c: Coincident(g87,g160)
    c: Coincident(g111,g135)
    c: Coincident(g158,g204)
    c: Coincident(g34,g41)
    c: Coincident(g84,g160)
    c: Coincident(g158,g245)
    c: Coincident(g111,g117)
    c: Coincident(g231,g254)
    c: Coincident(g84,g123)
    c: Coincident(g125,g245)
    c: Coincident(g50,g125)
    c: Coincident(g14,g123)
    c: Coincident(g117,g227)
    c: Coincident(g34,g62)
    c: Coincident(g14,g142)
    c: Coincident(g50,g97)
    c: Coincident(g0,g231)
    c: Coincident(g55,g97)
    c: Coincident(g120,g142)
    c: Coincident(g55,g59)
    c: Coincident(g59,g128)
    c: Coincident(g80,g254)
    c: Coincident(g128,g253)
    c: Coincident(g152,g253)
    c: Coincident(g152,g193)
    c: Coincident(g193,g194)
    c: Coincident(g45,g227)
    c: Coincident(g24,g120)
    c: Coincident(g53,g62)
    c: Coincident(g0,g136)
    c: Coincident(g45,g58)
    c: Coincident(g80,g201)
    c: Coincident(g136,g188)
    c: Coincident(g53,g235)
    c: Coincident(g47,g58)
    c: Coincident(g188,g256)
    c: Coincident(g82,g201)
    c: Coincident(g47,g69)
    c: Coincident(g8,g235)
    c: Coincident(g166,g256)
    c: Coincident(g82,g205)
    c: Coincident(g166,g186)
    c: Coincident(g13,g69)
    c: Coincident(g8,g39)
    c: Coincident(g13,g72)
    c: Coincident(g170,g186)
    c: Coincident(g72,g78)
    c: Coincident(g183,g205)
    c: Coincident(g157,g170)
    c: Coincident(g78,g246)
    c: Coincident(g39,g65)
    c: Coincident(g99,g246)
    c: Coincident(g157,g251)
    c: Coincident(g99,g124)
    c: Coincident(g126,g183)
    c: Coincident(g236,g251)
    c: Coincident(g124,g156)
    c: Coincident(g89,g236)
    c: Coincident(g156,g247)
    c: Coincident(g65,g118)
    c: Coincident(g191,g247)
    c: Coincident(g89,g240)
    c: Coincident(g113,g126)
    c: Coincident(g114,g191)
    c: Coincident(g1,g114)
    c: Coincident(g202,g240)
    c: Coincident(g48,g202)
    c: Coincident(g9,g113)
    c: Coincident(g118,g220)
    c: Coincident(g9,g249)
    c: Coincident(g220,g255)
    c: Coincident(g192,g249)
    c: Coincident(g214,g255)
    c: Coincident(g138,g192)
    c: Coincident(g42,g214)
    c: Coincident(g42,g238)
    c: Coincident(g138,g189)
    c: Coincident(g140,g238)
    c: Coincident(g174,g189)
    c: Coincident(g100,g140)
    c: Coincident(g159,g174)
    c: Coincident(g100,g242)
    c: Coincident(g12,g159)
    c: Coincident(g79,g242)
    c: Coincident(g12,g23)
    c: Coincident(g24,g103)
    c: Coincident(g103,g194)
    c: Coincident(g1,g203)
    c: Coincident(g48,g203)
    c: Coincident(g79,g164)
    c: Coincident(g23,g164)
FEATURE [App::Part] Board_Geoms_931
  Group = -> [Pcb_931,PCB_Sketch_931]
  Origin = -> Origin
FEATURE [Part::Feature] Shape  label="R21_C_0402_1005Metric_38c94f1f1ba7"
  Placement = pos=(189.8,-128.5,0) rot=(0,0,1;3.14159rad)
  shape: bbox 1 x 0.5 x 0.5 mm, 28 faces (baked)
FEATURE [App::Link] R21_C_0402_1005Metric_38c94f1f1ba7_ln_  label="R20_C_0402_1005Metric_7b8d80ad2dcc"
  LinkPlacement = pos=(189.9,-114.1,0) rot=(0,0,1;3.14159rad)
  LinkedObject = -> Shape
  Placement = pos=(189.9,-114.1,0) rot=(0,0,1;3.14159rad)
FEATURE [App::Link] R21_C_0402_1005Metric_38c94f1f1ba7_ln_001  label="C1_C_0402_1005Metric_d29c508b4b60"
  LinkPlacement = pos=(195.2,-70.7,0) rot=(0,0,1;0rad)
  LinkedObject = -> Shape
  Placement = pos=(195.2,-70.7,0) rot=(0,0,1;0rad)
FEATURE [Part::Feature] Shape001  label="R19_R_0402_1005Metric_9ca80ee487fc"
  Placement = pos=(194.8,-102.6,0) rot=(0,0,-1;1.5708rad)
  shape: bbox 0.5 x 1 x 0.35 mm, 26 faces (baked)
FEATURE [App::Link] R21_C_0402_1005Metric_38c94f1f1ba7_ln_002  label="C9_C_0402_1005Metric_a875c5e367f2"
  LinkPlacement = pos=(190.3,-80.1,0) rot=(0,0,-1;1.5708rad)
  LinkedObject = -> Shape
  Placement = pos=(190.3,-80.1,0) rot=(0,0,-1;1.5708rad)
FEATURE [Part::Feature] Shape002  label="D2_D_SMA_34cf3897dfc1"
  Placement = pos=(195.2,-118,0) rot=(0,0,-1;1.5708rad)
  shape: bbox 2.7 x 5 x 2.22 mm, 41 faces (baked)
FEATURE [Part::Feature] Shape003  label="C42_C_0603_1608Metric_3f0e18eb3bdb"
  Placement = pos=(197,-72.4,0) rot=(0,0,1;1.5708rad)
  shape: bbox 0.8 x 1.6 x 0.8 mm, 28 faces (baked)
FEATURE [Part::Feature] Shape004  label="SW3_Fillet_54ad2342c7e7"
  Placement = pos=(195.3,-140.21,0) rot=(0,0,1;3.14159rad)
  shape: bbox 8.3 x 20.48 x 8.6 mm, 32 faces (baked)
FEATURE [Part::Feature] Shape005  label="U5_SOT_223_0bc22c24d438"
  Placement = pos=(202.5,-74.4,0) rot=(0,0,1;0rad)
  shape: bbox 7 x 6.5 x 1.7 mm, 78 faces (baked)
FEATURE [App::Link] R19_R_0402_1005Metric_9ca80ee487fc_ln_  label="R2_R_0402_1005Metric_dea8e135976e"
  LinkPlacement = pos=(201.5,-68.7,0) rot=(0,0,1;1.5708rad)
  LinkedObject = -> Shape001
  Placement = pos=(201.5,-68.7,0) rot=(0,0,1;1.5708rad)
FEATURE [App::Link] C42_C_0603_1608Metric_3f0e18eb3bdb_ln_  label="C45_C_0603_1608Metric_d322fa890f2c"
  LinkPlacement = pos=(188.9,-123.4,0) rot=(0,0,1;0rad)
  LinkedObject = -> Shape003
  Placement = pos=(188.9,-123.4,0) rot=(0,0,1;0rad)
FEATURE [App::Link] R21_C_0402_1005Metric_38c94f1f1ba7_ln_003  label="C46_C_0402_1005Metric_a9bfb0d6892e"
  LinkPlacement = pos=(189.1,-100.1,0) rot=(0,0,1;0rad)
  LinkedObject = -> Shape
  Placement = pos=(189.1,-100.1,0) rot=(0,0,1;0rad)
FEATURE [App::Link] R19_R_0402_1005Metric_9ca80ee487fc_ln_001  label="R15_R_0402_1005Metric_e6cf502f8789"
  LinkPlacement = pos=(187.7,-106.9,0) rot=(0,0,-1;1.5708rad)
  LinkedObject = -> Shape001
  Placement = pos=(187.7,-106.9,0) rot=(0,0,-1;1.5708rad)
FEATURE [Part::Feature] Shape006  label="C44_C_1206_3216Metric_504a53cc2dd0"
  Placement = pos=(190.5,-133.025,0) rot=(0,0,-1;1.5708rad)
  shape: bbox 1.6 x 3.2 x 1.6 mm, 28 faces (baked)
FEATURE [App::Link] R21_C_0402_1005Metric_38c94f1f1ba7_ln_004  label="C18_C_0402_1005Metric_92a1be41be9e"
  LinkPlacement = pos=(189.4,-106.5,0) rot=(0,0,1;0rad)
  LinkedObject = -> Shape
  Placement = pos=(189.4,-106.5,0) rot=(0,0,1;0rad)
FEATURE [App::Link] R21_C_0402_1005Metric_38c94f1f1ba7_ln_005  label="C31_C_0402_1005Metric_578c4d3870ae"
  LinkPlacement = pos=(189,-90,0) rot=(0,0,1;3.14159rad)
  LinkedObject = -> Shape
  Placement = pos=(189,-90,0) rot=(0,0,1;3.14159rad)
FEATURE [App::Link] R19_R_0402_1005Metric_9ca80ee487fc_ln_002  label="R3_R_0402_1005Metric_969b0b0747f2"
  LinkPlacement = pos=(191.3,-80.09,0) rot=(0,0,-1;1.5708rad)
  LinkedObject = -> Shape001
  Placement = pos=(191.3,-80.09,0) rot=(0,0,-1;1.5708rad)
FEATURE [App::Link] R21_C_0402_1005Metric_38c94f1f1ba7_ln_006  label="C29_C_0402_1005Metric_878fa2face33"
  LinkPlacement = pos=(185.6,-86.9,0) rot=(0,0,1;1.5708rad)
  LinkedObject = -> Shape
  Placement = pos=(185.6,-86.9,0) rot=(0,0,1;1.5708rad)
FEATURE [Part::Feature] Shape007  label="U6_QFN-20-1EP_4x4mm_Pitch0.5mm_3f7a39cb167c"
  Placement = pos=(190.975,-103.35,0) rot=(0,0,1;1.5708rad)
  shape: bbox 4 x 4 x 0.77 mm, 134 faces (baked)
FEATURE [App::Link] R19_R_0402_1005Metric_9ca80ee487fc_ln_003  label="R18_R_0402_1005Metric_e9874ca0240e"
  LinkPlacement = pos=(195.4,-53,0) rot=(0,0,1;1.5708rad)
  LinkedObject = -> Shape001
  Placement = pos=(195.4,-53,0) rot=(0,0,1;1.5708rad)
FEATURE [App::Link] R19_R_0402_1005Metric_9ca80ee487fc_ln_004  label="R7_R_0402_1005Metric_0d6ee2aba382"
  LinkPlacement = pos=(196.1,-57,0) rot=(0,0,-1;1.5708rad)
  LinkedObject = -> Shape001
  Placement = pos=(196.1,-57,0) rot=(0,0,-1;1.5708rad)
FEATURE [Part::Feature] Shape008  label="L3_L_0402_1005Metric_7322f57e24a3"
  Placement = pos=(191.1,-99,0) rot=(0,0,1;3.14159rad)
  shape: bbox 1 x 0.5 x 0.5 mm, 28 faces (baked)
FEATURE [App::Link] C42_C_0603_1608Metric_3f0e18eb3bdb_ln_001  label="C26_C_0603_1608Metric_e24a75b1fd6c"
  LinkPlacement = pos=(196.7,-53.6,0) rot=(0,0,-1;1.5708rad)
  LinkedObject = -> Shape003
  Placement = pos=(196.7,-53.6,0) rot=(0,0,-1;1.5708rad)
FEATURE [App::Link] R21_C_0402_1005Metric_38c94f1f1ba7_ln_007  label="C41_C_0402_1005Metric_e05767d0328b"
  LinkPlacement = pos=(196.7,-101.5,0) rot=(0,0,1;1.5708rad)
  LinkedObject = -> Shape
  Placement = pos=(196.7,-101.5,0) rot=(0,0,1;1.5708rad)
FEATURE [App::Link] R19_R_0402_1005Metric_9ca80ee487fc_ln_005  label="R6_R_0402_1005Metric_11a2181a152e"
  LinkPlacement = pos=(195.1,-57,0) rot=(0,0,-1;1.5708rad)
  LinkedObject = -> Shape001
  Placement = pos=(195.1,-57,0) rot=(0,0,-1;1.5708rad)
FEATURE [App::Link] C44_C_1206_3216Metric_504a53cc2dd0_ln_  label="C15_C_1206_3216Metric_4eda32e8580f"
  LinkPlacement = pos=(204.5,-79.3,0) rot=(0,0,1;0rad)
  LinkedObject = -> Shape006
  Placement = pos=(204.5,-79.3,0) rot=(0,0,1;0rad)
FEATURE [App::Link] C44_C_1206_3216Metric_504a53cc2dd0_ln_001  label="C22_C_1206_3216Metric_2920babed859"
  LinkPlacement = pos=(204.4,-81.8,0) rot=(0,0,1;0rad)
  LinkedObject = -> Shape006
  Placement = pos=(204.4,-81.8,0) rot=(0,0,1;0rad)
FEATURE [App::Link] R19_R_0402_1005Metric_9ca80ee487fc_ln_006  label="R23_R_0402_1005Metric_7dfb490c449e"
  LinkPlacement = pos=(184.1,-52.41,0) rot=(0,0,1;1.5708rad)
  LinkedObject = -> Shape001
  Placement = pos=(184.1,-52.41,0) rot=(0,0,1;1.5708rad)
FEATURE [Part::Feature] Shape009  label="D516_LED_0603_1608Metric_23db4c450fc7"
  Placement = pos=(189.1,-126.2,0) rot=(0,0,1;1.5708rad)
  shape: bbox 0.8 x 1.6 x 1.1 mm, 50 faces (baked)
FEATURE [App::Link] R21_C_0402_1005Metric_38c94f1f1ba7_ln_008  label="C16_C_0402_1005Metric_ccc6f5fbae95"
  LinkPlacement = pos=(192.7,-132.7,0) rot=(0,0,1;1.5708rad)
  LinkedObject = -> Shape
  Placement = pos=(192.7,-132.7,0) rot=(0,0,1;1.5708rad)
FEATURE [App::Link] R21_C_0402_1005Metric_38c94f1f1ba7_ln_009  label="C20_C_0402_1005Metric_339430b002f9"
  LinkPlacement = pos=(204.7,-53.1,0) rot=(0,0,1;3.14159rad)
  LinkedObject = -> Shape
  Placement = pos=(204.7,-53.1,0) rot=(0,0,1;3.14159rad)
FEATURE [App::Link] R21_C_0402_1005Metric_38c94f1f1ba7_ln_010  label="C47_C_0402_1005Metric_af42fe187c16"
  LinkPlacement = pos=(195,-99.9,0) rot=(0,0,1;0rad)
  LinkedObject = -> Shape
  Placement = pos=(195,-99.9,0) rot=(0,0,1;0rad)
FEATURE [Part::Feature] Shape010  label="U8_SOT_23_1e3b1a0e5d43"
  Placement = pos=(193.9,-128,0) rot=(0,0,1;3.14159rad)
  shape: bbox 2.5 x 3 x 1.2 mm, 76 faces (baked)
FEATURE [App::Link] R21_C_0402_1005Metric_38c94f1f1ba7_ln_011  label="C6_C_0402_1005Metric_7f7ff18c55e3"
  LinkPlacement = pos=(190.5,-68.8,0) rot=(0,0,1;3.14159rad)
  LinkedObject = -> Shape
  Placement = pos=(190.5,-68.8,0) rot=(0,0,1;3.14159rad)
FEATURE [App::Link] D2_D_SMA_34cf3897dfc1_ln_  label="D1_D_SMA_3cb871b8a290"
  LinkPlacement = pos=(190.3,-109.8,0) rot=(0,0,1;3.14159rad)
  LinkedObject = -> Shape002
  Placement = pos=(190.3,-109.8,0) rot=(0,0,1;3.14159rad)
FEATURE [Part::Feature] Shape011  label="U3_QFN_56_1EP_7x7mm_P04mm_EP32x32mm_92a982e71d8d"
  Placement = pos=(189.6,-74.9,0) rot=(0,0,1;0rad)
  shape: bbox 7 x 7 x 0.95 mm, 350 faces (baked)
FEATURE [App::Link] R21_C_0402_1005Metric_38c94f1f1ba7_ln_012  label="C30_C_0402_1005Metric_cc59a400e17a"
  LinkPlacement = pos=(191,-90,0) rot=(0,0,1;3.14159rad)
  LinkedObject = -> Shape
  Placement = pos=(191,-90,0) rot=(0,0,1;3.14159rad)
FEATURE [App::Link] R21_C_0402_1005Metric_38c94f1f1ba7_ln_013  label="C13_C_0402_1005Metric_d2173120320b"
  LinkPlacement = pos=(198.8,-57.6,0) rot=(0,0,1;3.14159rad)
  LinkedObject = -> Shape
  Placement = pos=(198.8,-57.6,0) rot=(0,0,1;3.14159rad)
FEATURE [App::Link] L3_L_0402_1005Metric_7322f57e24a3_ln_  label="L4_L_0402_1005Metric_e4c50960bfc8"
  LinkPlacement = pos=(190.7,-97.6,0) rot=(0,0,1;0rad)
  LinkedObject = -> Shape008
  Placement = pos=(190.7,-97.6,0) rot=(0,0,1;0rad)
FEATURE [App::Link] R21_C_0402_1005Metric_38c94f1f1ba7_ln_014  label="C2_C_0402_1005Metric_4b4f118f5010"
  LinkPlacement = pos=(185.6,-81.3,0) rot=(0,0,1;3.14159rad)
  LinkedObject = -> Shape
  Placement = pos=(185.6,-81.3,0) rot=(0,0,1;3.14159rad)
FEATURE [App::Link] D516_LED_0603_1608Metric_23db4c450fc7_ln_  label="D517_LED_0603_1608Metric_b24ae36cc63a"
  LinkPlacement = pos=(190.7,-126.2,0) rot=(0,0,1;1.5708rad)
  LinkedObject = -> Shape009
  Placement = pos=(190.7,-126.2,0) rot=(0,0,1;1.5708rad)
FEATURE [App::Link] R21_C_0402_1005Metric_38c94f1f1ba7_ln_015  label="C10_C_0402_1005Metric_25fd1e42a1bf"
  LinkPlacement = pos=(186.1,-69.6,0) rot=(0,0,1;1.5708rad)
  LinkedObject = -> Shape
  Placement = pos=(186.1,-69.6,0) rot=(0,0,1;1.5708rad)
FEATURE [App::Link] R21_C_0402_1005Metric_38c94f1f1ba7_ln_016  label="C33_C_0402_1005Metric_872bb8822931"
  LinkPlacement = pos=(204.2,-51.5,0) rot=(0,0,-1;1.5708rad)
  LinkedObject = -> Shape
  Placement = pos=(204.2,-51.5,0) rot=(0,0,-1;1.5708rad)
FEATURE [App::Link] R21_C_0402_1005Metric_38c94f1f1ba7_ln_017  label="C43_C_0402_1005Metric_b465c88a99c7"
  LinkPlacement = pos=(202.2,-129.1,0) rot=(0,0,-1;1.5708rad)
  LinkedObject = -> Shape
  Placement = pos=(202.2,-129.1,0) rot=(0,0,-1;1.5708rad)
FEATURE [App::Link] R19_R_0402_1005Metric_9ca80ee487fc_ln_007  label="R4_R_0402_1005Metric_18a2017ffd4b"
  LinkPlacement = pos=(194,-57,0) rot=(0,0,-1;1.5708rad)
  LinkedObject = -> Shape001
  Placement = pos=(194,-57,0) rot=(0,0,-1;1.5708rad)
FEATURE [App::Link] C44_C_1206_3216Metric_504a53cc2dd0_ln_002  label="C25_C_1206_3216Metric_a9b05d8d3b1b"
  LinkPlacement = pos=(199.6,-132.5,0) rot=(0,0,1;0rad)
  LinkedObject = -> Shape006
  Placement = pos=(199.6,-132.5,0) rot=(0,0,1;0rad)
FEATURE [Part::Feature] Shape012  label="Y1_Crystal_SMD_3225-4Pin_3.2x2.5mm_5bc66405eca2"
  Placement = pos=(186.9,-83.7,0) rot=(0,0,1;0rad)
  shape: bbox 3.2 x 2.501 x 0.64 mm, 28 faces (baked)
FEATURE [App::Link] R19_R_0402_1005Metric_9ca80ee487fc_ln_008  label="R16_R_0402_1005Metric_1ac23e3eb529"
  LinkPlacement = pos=(205.3,-51.5,0) rot=(0,0,-1;1.5708rad)
  LinkedObject = -> Shape001
  Placement = pos=(205.3,-51.5,0) rot=(0,0,-1;1.5708rad)
FEATURE [App::Link] R19_R_0402_1005Metric_9ca80ee487fc_ln_009  label="Q1_R_0402_1005Metric_19db146f615e"
  LinkPlacement = pos=(204.7,-50,0) rot=(0,0,1;0rad)
  LinkedObject = -> Shape001
  Placement = pos=(204.7,-50,0) rot=(0,0,1;0rad)
FEATURE [App::Link] U8_SOT_23_1e3b1a0e5d43_ln_  label="Q2_SOT_23_816b0a6423d4"
  LinkPlacement = pos=(191.1,-56.8,0) rot=(0,0,1;1.5708rad)
  LinkedObject = -> Shape010
  Placement = pos=(191.1,-56.8,0) rot=(0,0,1;1.5708rad)
FEATURE [App::Link] R21_C_0402_1005Metric_38c94f1f1ba7_ln_018  label="C24_C_0402_1005Metric_c74ed45d8278"
  LinkPlacement = pos=(196.3,-103.1,0) rot=(0,0,1;0rad)
  LinkedObject = -> Shape
  Placement = pos=(196.3,-103.1,0) rot=(0,0,1;0rad)
FEATURE [App::Link] C44_C_1206_3216Metric_504a53cc2dd0_ln_003  label="C35_C_1206_3216Metric_0a151451740c"
  LinkPlacement = pos=(201.1,-105.5,0) rot=(0,0,1;1.5708rad)
  LinkedObject = -> Shape006
  Placement = pos=(201.1,-105.5,0) rot=(0,0,1;1.5708rad)
FEATURE [App::Link] R21_C_0402_1005Metric_38c94f1f1ba7_ln_019  label="R22_C_0402_1005Metric_0e379b04b221"
  LinkPlacement = pos=(195.3,-65,0) rot=(0,0,1;0rad)
  LinkedObject = -> Shape
  Placement = pos=(195.3,-65,0) rot=(0,0,1;0rad)
FEATURE [App::Link] R19_R_0402_1005Metric_9ca80ee487fc_ln_010  label="R17_R_0402_1005Metric_c84f106557fc"
  LinkPlacement = pos=(193.4,-52.99,0) rot=(0,0,1;1.5708rad)
  LinkedObject = -> Shape001
  Placement = pos=(193.4,-52.99,0) rot=(0,0,1;1.5708rad)
FEATURE [App::Link] R21_C_0402_1005Metric_38c94f1f1ba7_ln_020  label="C34_C_0402_1005Metric_69e14d7ecb16"
  LinkPlacement = pos=(200.7,-51.3,0) rot=(0,0,-1;1.5708rad)
  LinkedObject = -> Shape
  Placement = pos=(200.7,-51.3,0) rot=(0,0,-1;1.5708rad)
FEATURE [App::Link] R21_C_0402_1005Metric_38c94f1f1ba7_ln_021  label="C32_C_0402_1005Metric_dab31895c2db"
  LinkPlacement = pos=(187,-90,0) rot=(0,0,1;3.14159rad)
  LinkedObject = -> Shape
  Placement = pos=(187,-90,0) rot=(0,0,1;3.14159rad)
FEATURE [App::Link] R21_C_0402_1005Metric_38c94f1f1ba7_ln_022  label="C23_C_0402_1005Metric_a91c703b8113"
  LinkPlacement = pos=(195,-100.9,0) rot=(0,0,1;3.14159rad)
  LinkedObject = -> Shape
  Placement = pos=(195,-100.9,0) rot=(0,0,1;3.14159rad)
FEATURE [Part::Feature] Shape013  label="J4_PinHeader_2x07_P127mm_Vertical_bf31e59c633b"
  Placement = pos=(194.765,-81.49,0) rot=(0,0,1;0rad)
  shape: bbox 3.4 x 8.89 x 6.3 mm, 298 faces (baked)
FEATURE [App::Link] R21_C_0402_1005Metric_38c94f1f1ba7_ln_023  label="C11_C_0402_1005Metric_ee0f1353bdd2"
  LinkPlacement = pos=(192.4,-68.8,0) rot=(0,0,1;0rad)
  LinkedObject = -> Shape
  Placement = pos=(192.4,-68.8,0) rot=(0,0,1;0rad)
FEATURE [App::Link] R19_R_0402_1005Metric_9ca80ee487fc_ln_011  label="R12_R_0402_1005Metric_1dd42002f4d0"
  LinkPlacement = pos=(200.1,-129.09,0) rot=(0,0,1;1.5708rad)
  LinkedObject = -> Shape001
  Placement = pos=(200.1,-129.09,0) rot=(0,0,1;1.5708rad)
FEATURE [App::Link] R21_C_0402_1005Metric_38c94f1f1ba7_ln_024  label="C27_C_0402_1005Metric_39aa6632ecb3"
  LinkPlacement = pos=(192.72,-97.6,0) rot=(0,0,1;0rad)
  LinkedObject = -> Shape
  Placement = pos=(192.72,-97.6,0) rot=(0,0,1;0rad)
FEATURE [App::Link] R19_R_0402_1005Metric_9ca80ee487fc_ln_012  label="R5_R_0402_1005Metric_a55a78cb6167"
  LinkPlacement = pos=(197.2,-57,0) rot=(0,0,-1;1.5708rad)
  LinkedObject = -> Shape001
  Placement = pos=(197.2,-57,0) rot=(0,0,-1;1.5708rad)
FEATURE [App::Link] R19_R_0402_1005Metric_9ca80ee487fc_ln_013  label="R1_R_0402_1005Metric_f5b816f9472f"
  LinkPlacement = pos=(199.8,-69.2,0) rot=(0,0,1;0rad)
  LinkedObject = -> Shape001
  Placement = pos=(199.8,-69.2,0) rot=(0,0,1;0rad)
FEATURE [App::Link] D516_LED_0603_1608Metric_23db4c450fc7_ln_001  label="D518_LED_0603_1608Metric_9ded9605b13f"
  LinkPlacement = pos=(195.4,-63.5,0) rot=(0,0,1;0rad)
  LinkedObject = -> Shape009
  Placement = pos=(195.4,-63.5,0) rot=(0,0,1;0rad)
FEATURE [App::Link] C44_C_1206_3216Metric_504a53cc2dd0_ln_004  label="C21_C_1206_3216Metric_429a80aec131"
  LinkPlacement = pos=(194.9,-112.9,0) rot=(0,0,1;3.14159rad)
  LinkedObject = -> Shape006
  Placement = pos=(194.9,-112.9,0) rot=(0,0,1;3.14159rad)
FEATURE [Part::Feature] Shape014  label="U9_SOT_23_6_c7a49d86fbfe"
  Placement = pos=(188.6,-87.6,0) rot=(0,0,1;3.14159rad)
  shape: bbox 2.8 x 2.9 x 1.55 mm, 124 faces (baked)
FEATURE [App::Link] R21_C_0402_1005Metric_38c94f1f1ba7_ln_025  label="C17_C_0402_1005Metric_54b876e493f1"
  LinkPlacement = pos=(189.4,-107.5,0) rot=(0,0,1;0rad)
  LinkedObject = -> Shape
  Placement = pos=(189.4,-107.5,0) rot=(0,0,1;0rad)
FEATURE [Part::Feature] Shape015  label="SW1_SW_SPST_PTS645_03fdbfd9ae36"
  Placement = pos=(200.6,-63,0) rot=(0,0,-1;1.5708rad)
  shape: bbox 6 x 9 x 4.3 mm, 97 faces (baked)
FEATURE [App::Link] R19_R_0402_1005Metric_9ca80ee487fc_ln_014  label="R24_R_0402_1005Metric_04ceae6545c3"
  LinkPlacement = pos=(188.2,-57.7,0) rot=(0,0,-1;1.5708rad)
  LinkedObject = -> Shape001
  Placement = pos=(188.2,-57.7,0) rot=(0,0,-1;1.5708rad)
FEATURE [App::Link] Y1_Crystal_SMD_3225_4Pin_3_2x2_5mm_5bc66405eca2_ln_  label="Y2_Crystal_SMD_3225-4Pin_3.2x2.5mm_c0e7deee875b"
  LinkPlacement = pos=(195.8,-105.9,0) rot=(0,0,1;1.5708rad)
  LinkedObject = -> Shape012
  Placement = pos=(195.8,-105.9,0) rot=(0,0,1;1.5708rad)
FEATURE [App::Link] R19_R_0402_1005Metric_9ca80ee487fc_ln_015  label="R10_R_0402_1005Metric_299a858bebda"
  LinkPlacement = pos=(195.5,-77.1,0) rot=(0,0,1;1.5708rad)
  LinkedObject = -> Shape001
  Placement = pos=(195.5,-77.1,0) rot=(0,0,1;1.5708rad)
FEATURE [App::Link] R19_R_0402_1005Metric_9ca80ee487fc_ln_016  label="R9_R_0402_1005Metric_84cfa7eb0e8e"
  LinkPlacement = pos=(198.9,-129.1,0) rot=(0,0,-1;1.5708rad)
  LinkedObject = -> Shape001
  Placement = pos=(198.9,-129.1,0) rot=(0,0,-1;1.5708rad)
FEATURE [App::Link] R21_C_0402_1005Metric_38c94f1f1ba7_ln_026  label="C28_C_0402_1005Metric_fdbb3c7674a5"
  LinkPlacement = pos=(194.2,-98.1,0) rot=(0,0,1;1.5708rad)
  LinkedObject = -> Shape
  Placement = pos=(194.2,-98.1,0) rot=(0,0,1;1.5708rad)
FEATURE [App::Link] R19_R_0402_1005Metric_9ca80ee487fc_ln_017  label="R11_R_0402_1005Metric_60fb483f3fd5"
  LinkPlacement = pos=(196.7,-77.1,0) rot=(0,0,-1;1.5708rad)
  LinkedObject = -> Shape001
  Placement = pos=(196.7,-77.1,0) rot=(0,0,-1;1.5708rad)
FEATURE [App::Link] R21_C_0402_1005Metric_38c94f1f1ba7_ln_027  label="C4_C_0402_1005Metric_564747b89293"
  LinkPlacement = pos=(187.92,-81.4,0) rot=(0,0,1;0rad)
  LinkedObject = -> Shape
  Placement = pos=(187.92,-81.4,0) rot=(0,0,1;0rad)
FEATURE [Part::Feature] Shape016  label="L1_Sf㱟fd_sp_e828286b0ac3"
  Placement = pos=(200.4,-114.7,0) rot=(0,0,1;1.5708rad)
  shape: bbox 7.058 x 7.058 x 2.5 mm, 79 faces (baked)
FEATURE [App::Link] L3_L_0402_1005Metric_7322f57e24a3_ln_001  label="L2_L_0402_1005Metric_cbc56b11f79b"
  LinkPlacement = pos=(192,-100.1,0) rot=(0,0,1;3.14159rad)
  LinkedObject = -> Shape008
  Placement = pos=(192,-100.1,0) rot=(0,0,1;3.14159rad)
FEATURE [App::Link] R19_R_0402_1005Metric_9ca80ee487fc_ln_018  label="R8_R_0402_1005Metric_044c423f79ff"
  LinkPlacement = pos=(197.8,-129.1,0) rot=(0,0,1;1.5708rad)
  LinkedObject = -> Shape001
  Placement = pos=(197.8,-129.1,0) rot=(0,0,1;1.5708rad)
FEATURE [App::Link] R21_C_0402_1005Metric_38c94f1f1ba7_ln_028  label="C5_C_0402_1005Metric_ff954b7ecdeb"
  LinkPlacement = pos=(190.5,-69.9,0) rot=(0,0,1;3.14159rad)
  LinkedObject = -> Shape
  Placement = pos=(190.5,-69.9,0) rot=(0,0,1;3.14159rad)
FEATURE [App::Link] R19_R_0402_1005Metric_9ca80ee487fc_ln_019  label="R14_R_0402_1005Metric_07a2d9395c6f"
  LinkPlacement = pos=(206.4,-51.5,0) rot=(0,0,-1;1.5708rad)
  LinkedObject = -> Shape001
  Placement = pos=(206.4,-51.5,0) rot=(0,0,-1;1.5708rad)
FEATURE [App::Link] R19_R_0402_1005Metric_9ca80ee487fc_ln_020  label="R13_R_0402_1005Metric_6ddea6fc7991"
  LinkPlacement = pos=(201.1,-129.1,0) rot=(0,0,-1;1.5708rad)
  LinkedObject = -> Shape001
  Placement = pos=(201.1,-129.1,0) rot=(0,0,-1;1.5708rad)
FEATURE [App::Part] Top_931
  Group = -> [Shape,R21_C_0402_1005Metric_38c94f1f1ba7_ln_,R21_C_0402_1005Metric_38c94f1f1ba7_ln_001,Shape001,R21_C_0402_1005Metric_38c94f1f1ba7_ln_002,Shape002,Shape003,Shape004,Shape005,R19_R_0402_1005Metric_9ca80ee487fc_ln_,C42_C_0603_1608Metric_3f0e18eb3bdb_ln_,R21_C_0402_1005Metric_38c94f1f1ba7_ln_003,R19_R_0402_1005Metric_9ca80ee487fc_ln_001,Shape006,R21_C_0402_1005Metric_38c94f1f1ba7_ln_004,+66 more]
  Origin = -> Origin003
FEATURE [Part::Feature] Shape017  label="BT1_MPD_BH_18650_PC2_17c3f7ae5d37"
  Placement = pos=(195.3,-132,-1.6) rot=(0.707107,0.707107,0;3.14159rad)
  shape: bbox 20.9 x 77.7 x 22.2 mm, 62 faces (baked)
FEATURE [Part::Feature] Shape018  label="J1_USB_Mini-B_Lumberg_2486_01_Horizontal_f06c414dff7d"
  Placement = pos=(195.3,-50.6,-1.6) rot=(1,0,0;3.14159rad)
  shape: bbox 9.9 x 9.2 x 4.997 mm, 472 faces (baked)
FEATURE [App::Part] Bot_931
  Group = -> [Shape017,Shape018]
  Origin = -> Origin004
FEATURE [App::Part] Step_Models_931
  Group = -> [Top_931,Bot_931]
  Origin = -> Origin002
FEATURE [App::Part] Board_931  label="ButterflyBadge"
  Group = -> [Local_CS_931,Board_Geoms_931,Step_Models_931]
  Origin = -> Origin001
